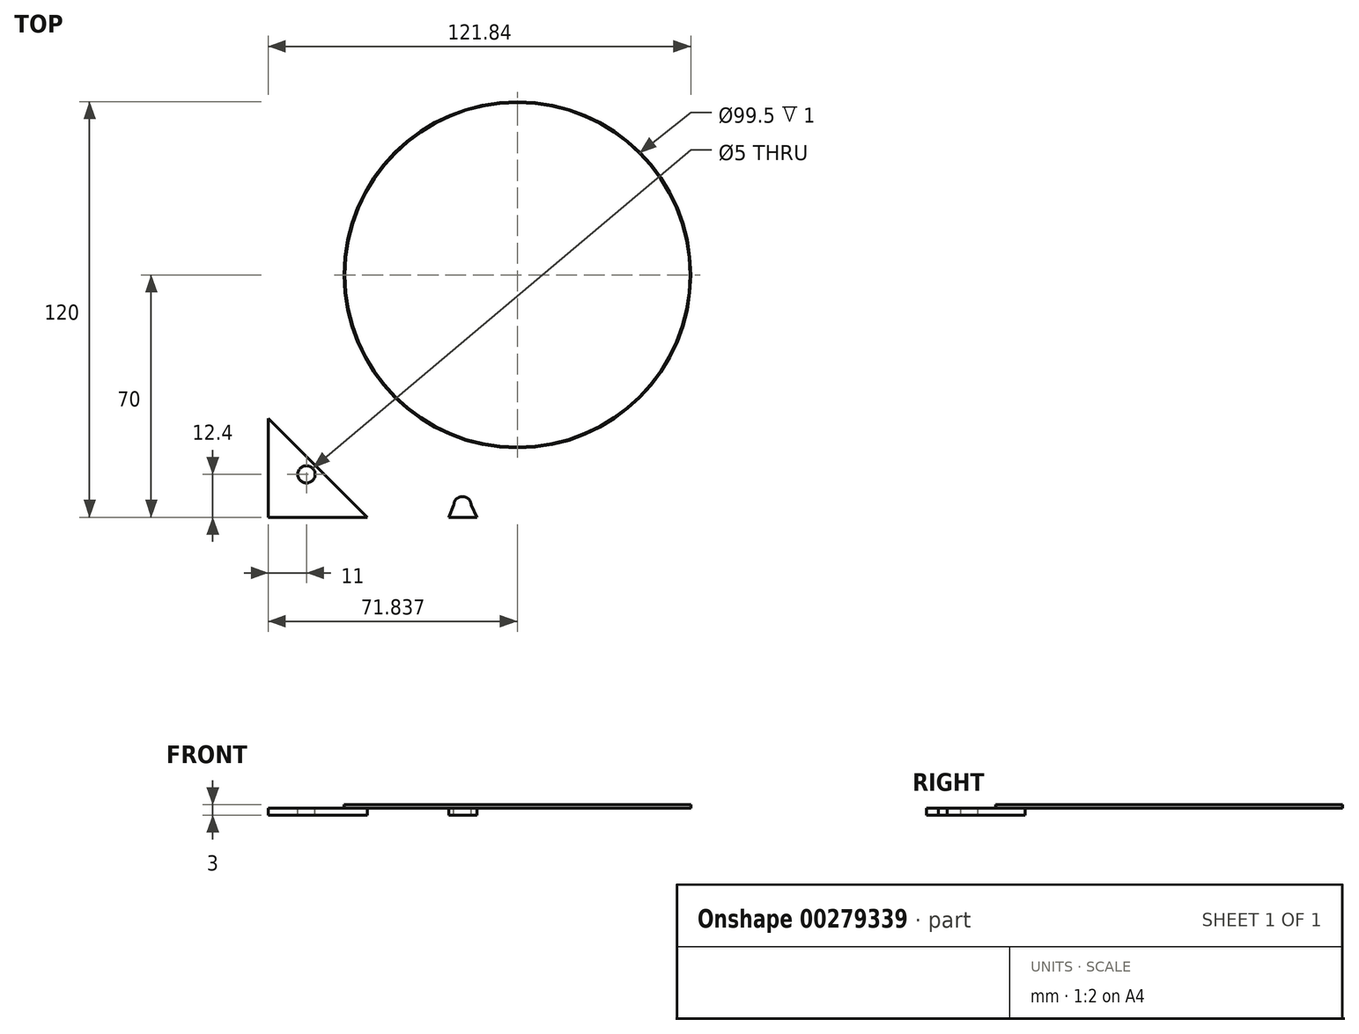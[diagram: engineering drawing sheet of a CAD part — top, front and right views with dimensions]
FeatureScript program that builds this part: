
annotation { "Feature Type Name" : "Feature", "Feature Type Description" : "" }
export const myFeature = defineFeature(function(context is Context, id is Id, definition is map)
    precondition{}
    {
        {
            var Q0;
            Q0=qCreatedBy(makeId("Top.planeOp"),FACE);
            var sketch = newSketch(context, id + "F0", { "sketchPlane" : qUnion([Q0])});
            skLineSegment(sketch, "E0.bottom", {"start": v(75, 70) * mm, "end": v(-75, 70) * mm});
            skLineSegment(sketch, "E0.top", {"start": v(75, -70) * mm, "end": v(-75, -70) * mm});
            skLineSegment(sketch, "E0.left", {"start": v(75, 70) * mm, "end": v(75, -70) * mm});
            skLineSegment(sketch, "E0.right", {"start": v(-75, 70) * mm, "end": v(-75, -70) * mm});
            skPoint(sketch, "E0.middle", {"position": v(0, 0) * mm});
            skSolve(sketch);
        }
        {
            var Q0;
            Q0=qSketchRegion(id+"F0",true);
            extrude(context, id + "F1", {"entities" : qUnion([Q0]), "depth" : 2 * mm});
        }
        {
            var Q0;
            Q0=makeQuery(id+"F1.opExtrude","CAP_FACE",FACE,{"disambiguationData":[OSD([sQuery(id+"F0.wireOp",EDGE,"E0.bottom"),sQuery(id+"F0.wireOp",EDGE,"E0.top"),sQuery(id+"F0.wireOp",EDGE,"E0.left"),sQuery(id+"F0.wireOp",EDGE,"E0.right")])],"isStart":false});
            var sketch = newSketch(context, id + "F2", { "sketchPlane" : qUnion([Q0])});
            skArc(sketch, "E1", {"start": v(-67.18, 6.35) * mm, "mid": v(-67.92, 8.12) * mm, "end": v(-69.68, 8.85) * mm});
            skArc(sketch, "E2.MirrorC", {"start": v(-67.18, -6.35) * mm, "mid": v(-67.92, -8.12) * mm, "end": v(-69.68, -8.85) * mm});
            skArc(sketch, "E3", {"start": v(-21.5, 66.52) * mm, "mid": v(-19, 64) * mm, "end": v(-16.5, 66.52) * mm});
            skCircle(sketch, "E4", {"center": v(-64, 57.6) * mm, "radius": 2.5 * mm});
            skArc(sketch, "E5.MirrorC", {"start": v(-21.5, -66.52) * mm, "mid": v(-19, -64) * mm, "end": v(-16.5, -66.52) * mm});
            skCircle(sketch, "E6.MirrorC", {"center": v(-64, -57.6) * mm, "radius": 2.5 * mm});
            skLineSegment(sketch, "E7", {"start": v(-21.5, 66.52) * mm, "end": v(-22.94, 70) * mm});
            skLineSegment(sketch, "E8.MirrorCS", {"start": v(-16.5, 66.52) * mm, "end": v(-14.88, 70) * mm});
            skLineSegment(sketch, "E9.MirrorCS", {"start": v(-16.5, -66.52) * mm, "end": v(-14.88, -70) * mm});
            skLineSegment(sketch, "E10.MirrorCS", {"start": v(-21.5, -66.52) * mm, "end": v(-22.94, -70) * mm});
            skLineSegment(sketch, "E11", {"start": v(-46.5, 70) * mm, "end": v(-75, 41.5) * mm});
            skLineSegment(sketch, "E12.MirrorCS", {"start": v(-46.5, -70) * mm, "end": v(-75, -41.5) * mm});
            skLineSegment(sketch, "E13", {"start": v(-69.68, 8.85) * mm, "end": v(-75, 8.85) * mm});
            skLineSegment(sketch, "E14", {"start": v(-67.18, -6.35) * mm, "end": v(-67.18, 6.35) * mm});
            skLineSegment(sketch, "E15.MirrorCS", {"start": v(-69.68, -8.85) * mm, "end": v(-75, -8.85) * mm});
            skSolve(sketch);
        }
        {
            var Q0;
            Q0=qSketchRegion(id+"F2",true);
            var Q1;
            Q1=makeQuery(id+"F2.imprint","IMPRINT",FACE,{"disambiguationData":[TD([[makeQuery(id+"F2.imprint","IMPRINT",EDGE,{"derivedFrom":sQuery(id+"F2.wireOp",EDGE,"E4")}),-1.0]])]});
            var Q2;
            Q2=makeQuery(id+"F2.imprint","IMPRINT",FACE,{"disambiguationData":[TD([[makeQuery(id+"F2.imprint","IMPRINT",EDGE,{"derivedFrom":sQuery(id+"F2.wireOp",EDGE,"E1")}),1.0]])]});
            var Q3;
            Q3=makeQuery(id+"F2.imprint","IMPRINT",FACE,{"disambiguationData":[TD([[makeQuery(id+"F2.imprint","IMPRINT",EDGE,{"derivedFrom":sQuery(id+"F2.wireOp",EDGE,"E5.MirrorC")}),-1.0]])]});
            var Q4;
            Q4=makeQuery(id+"F2.imprint","IMPRINT",FACE,{"disambiguationData":[TD([[makeQuery(id+"F2.imprint","IMPRINT",EDGE,{"derivedFrom":sQuery(id+"F2.wireOp",EDGE,"E3")}),1.0]])]});
            var Q5;
            Q5=makeQuery(id+"F2.imprint","IMPRINT",FACE,{"disambiguationData":[TD([[makeQuery(id+"F2.imprint","IMPRINT",EDGE,{"derivedFrom":sQuery(id+"F2.wireOp",EDGE,"E6.MirrorC")}),1.0]])]});
            extrude(context, id + "F3", {"entities" : qUnion([Q0, Q1, Q2, Q3, Q4, Q5]), "operationType" : NewBodyOperationType.REMOVE, "oppositeDirection" : true, "depth" : 5 * mm});
        }
        {
            var Q0;
            Q0=makeQuery(id+"F1.opExtrude","CAP_FACE",FACE,{"disambiguationData":[OSD([sQuery(id+"F0.wireOp",EDGE,"E0.bottom"),sQuery(id+"F0.wireOp",EDGE,"E0.top"),sQuery(id+"F0.wireOp",EDGE,"E0.left"),sQuery(id+"F0.wireOp",EDGE,"E0.right")])],"isStart":false});
            var sketch = newSketch(context, id + "F4", { "sketchPlane" : qUnion([Q0])});
            skCircle(sketch, "E16", {"center": v(-3.16, 0) * mm, "radius": 49.75 * mm});
            skCircle(sketch, "E17", {"center": v(-3.16, 0) * mm, "radius": 50 * mm});
            skSolve(sketch);
        }
        {
            var Q0;
            Q0=makeQuery(id+"F4.imprint","IMPRINT",FACE,{"disambiguationData":[TD([[makeQuery(id+"F4.imprint","IMPRINT",EDGE,{"derivedFrom":sQuery(id+"F4.wireOp",EDGE,"E16")}),-1.0]])]});
            extrude(context, id + "F5", {"entities" : qUnion([Q0]), "operationType" : NewBodyOperationType.ADD, "depth" : 1 * mm});
        }
    });
